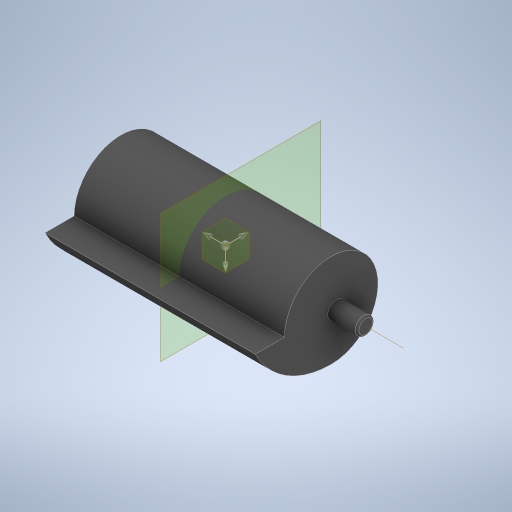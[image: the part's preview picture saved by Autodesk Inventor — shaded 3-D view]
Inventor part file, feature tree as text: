
AUTODESK INVENTOR PART (.ipt)
format: ipt  version: 2024 (Build 280153000, 153)  size: 586,752 bytes
history: native  units: in
note: dims shown in document units (in); Inventor stores cm internally (conversion verified against a paired STEP export)
features: extrude x3, sketch x2, plane x1, other x1, fillet x1
ambient origin geometry x8: Origin, YZ Plane, XZ Plane, XY Plane, X Axis, Y Axis, Z Axis, Center Point
bodies: Solid1 (feature_tree)
feature tree (8):
  extrude  "Extrusion1"  Depth=3.6in TaperAngle=0.0deg
  plane  "Work Plane1"
  sketch  "Sketch2"  dims[d5=0.23in d6=0.3in d7=0.5in d8=0.0in d9=0.55in d10=0.0in d11=0.18in d12=0.5in d13=0.0312in]
  extrude  "Extrusion2"  Depth=0.0312in
  extrude  "Extrusion3"  Depth=0.5in TaperAngle=0.0deg
  other  "Work Axis1"
  fillet  "Fillet1"  Radius=0.55in
  sketch  "Sketch1"  dims[d0=1.6in d2=3.6in d3=0.0in]
